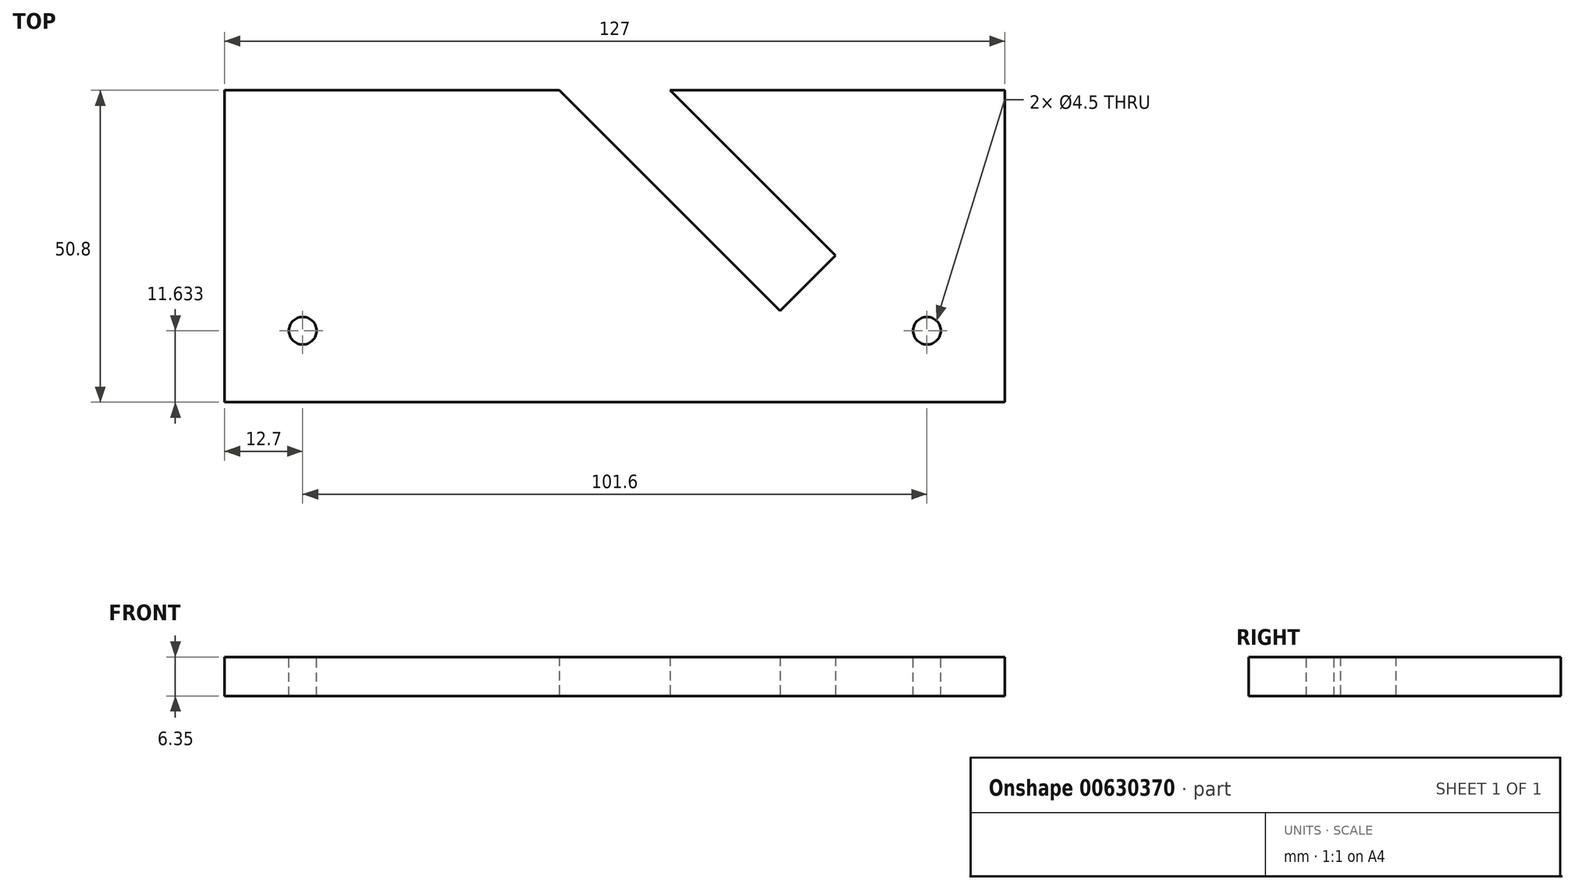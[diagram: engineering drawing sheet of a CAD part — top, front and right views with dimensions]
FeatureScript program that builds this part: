
annotation { "Feature Type Name" : "Feature", "Feature Type Description" : "" }
export const myFeature = defineFeature(function(context is Context, id is Id, definition is map)
    precondition{}
    {
        {
            var Q0;
            Q0=qCreatedBy(makeId("Top.planeOp"),FACE);
            var sketch = newSketch(context, id + "F0", { "sketchPlane" : qUnion([Q0])});
            skLineSegment(sketch, "E0.bottom", {"start": v(-63.5, 25.4) * mm, "end": v(-9.02, 25.4) * mm});
            skLineSegment(sketch, "E0.top", {"start": v(-63.5, -25.4) * mm, "end": v(63.5, -25.4) * mm});
            skLineSegment(sketch, "E0.left", {"start": v(-63.5, 25.4) * mm, "end": v(-63.5, -25.4) * mm});
            skLineSegment(sketch, "E0.right", {"start": v(63.5, 25.4) * mm, "end": v(63.5, -25.4) * mm});
            skPoint(sketch, "E0.middle", {"position": v(0, 0) * mm});
            skLineSegment(sketch, "E1", {"start": v(-9.02, 25.4) * mm, "end": v(26.9, -10.52) * mm});
            skLineSegment(sketch, "E2", {"start": v(26.9, -10.52) * mm, "end": v(35.92, -1.5) * mm});
            skLineSegment(sketch, "E3", {"start": v(35.92, -1.5) * mm, "end": v(9.02, 25.4) * mm});
            skLineSegment(sketch, "E4.trimOffspring", {"start": v(9.02, 25.4) * mm, "end": v(63.5, 25.4) * mm});
            skLineSegment(sketch, "E5", {"start": v(-9.02, 25.4) * mm, "end": v(9.02, 25.4) * mm, "construction": true});
            skPoint(sketch, "E6", {"position": v(0, 25.4) * mm});
            skSolve(sketch);
        }
        {
            var Q0;
            Q0 = qSketchRegion(id + "F0", true);
            extrude(context, id + "F1", {"entities" : qUnion([Q0]), "depth" : 6.35 * mm, "offsetDistance" : 25.4 * mm});
        }
        {
            var Q0;
            Q0=makeQuery(id+"F1.opExtrude","CAP_FACE",FACE,{"disambiguationData":[OSD([sQuery(id+"F0.wireOp",EDGE,"E0.bottom"),sQuery(id+"F0.wireOp",EDGE,"E0.top"),sQuery(id+"F0.wireOp",EDGE,"E0.left"),sQuery(id+"F0.wireOp",EDGE,"E0.right"),sQuery(id+"F0.wireOp",EDGE,"E1"),sQuery(id+"F0.wireOp",EDGE,"E2"),sQuery(id+"F0.wireOp",EDGE,"E3"),sQuery(id+"F0.wireOp",EDGE,"E4.trimOffspring")])],"isStart":false});
            var sketch = newSketch(context, id + "F2", { "sketchPlane" : qUnion([Q0])});
            skLineSegment(sketch, "E7", {"start": v(-50.8, -25.4) * mm, "end": v(-50.8, -13.77) * mm, "construction": true});
            skLineSegment(sketch, "E8", {"start": v(50.8, -25.4) * mm, "end": v(50.8, -13.77) * mm, "construction": true});
            skPoint(sketch, "E9", {"position": v(-50.8, -13.77) * mm});
            skPoint(sketch, "E10", {"position": v(50.8, -13.77) * mm});
            skSolve(sketch);
        }
        {
            var Q0;
            Q0=sQuery(id+"F2.wireOp",VERTEX,"E7.end");
            var Q1;
            Q1=sQuery(id+"F2.wireOp",VERTEX,"E10");
            var Q2;
            Q2=makeQuery(id+"F1.opExtrude","SWEPT_BODY",BODY,{"disambiguationData":[OSD([sQuery(id+"F0.wireOp",EDGE,"E0.bottom"),sQuery(id+"F0.wireOp",EDGE,"E0.top"),sQuery(id+"F0.wireOp",EDGE,"E0.left"),sQuery(id+"F0.wireOp",EDGE,"E0.right"),sQuery(id+"F0.wireOp",EDGE,"E1"),sQuery(id+"F0.wireOp",EDGE,"E2"),sQuery(id+"F0.wireOp",EDGE,"E3"),sQuery(id+"F0.wireOp",EDGE,"E4.trimOffspring")])]});
            hole(context, id + "F3", {"style" : HoleStyle.SIMPLE, "endStyle" : HoleEndStyle.THROUGH, "standardTappedOrClearance" : lookupTablePath({ "standard" : "ANSI", "fit" : "Normal (ASME)", "size" : "#8", "type" : "Clearance" }), "standardBlindInLast" : lookupTablePath({ "fit" : "Free", "standard" : "ANSI", "size" : "#8", "type" : "Clearance" }), "holeDiameter" : 4.5 * mm, "majorDiameter" : 6.35 * mm, "isTappedThrough" : true, "tappedDepth" : 12.7 * mm, "tapClearance" : 3, "locations" : qUnion([Q0, Q1]), "scope" : qUnion([Q2])});
        }
    });
